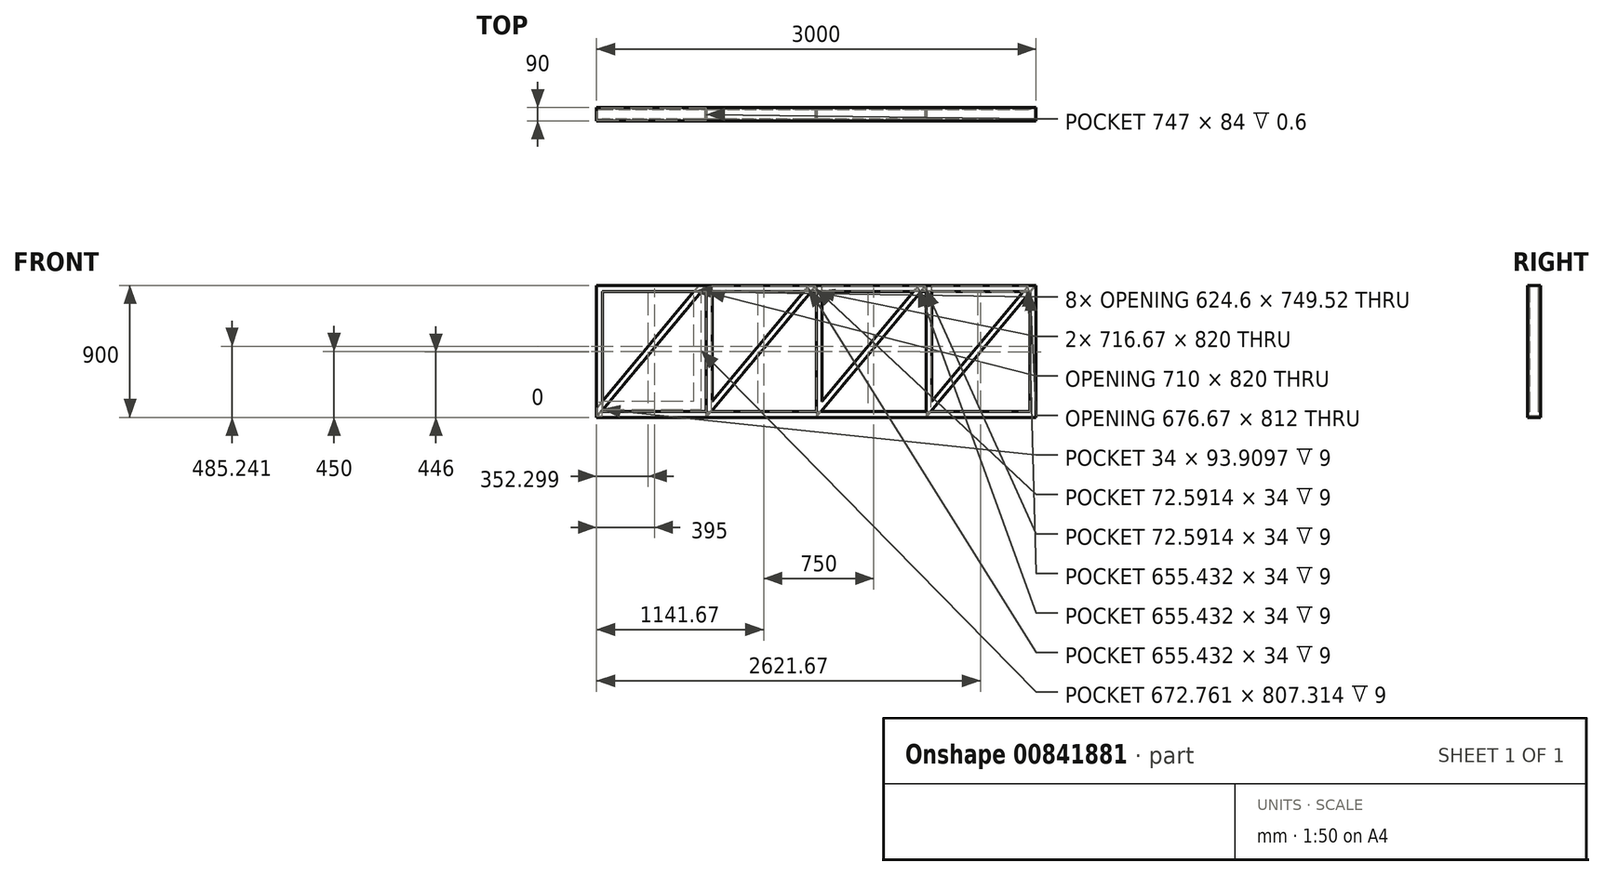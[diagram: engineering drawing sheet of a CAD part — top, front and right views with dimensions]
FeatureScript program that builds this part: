
annotation { "Feature Type Name" : "Feature", "Feature Type Description" : "" }
export const myFeature = defineFeature(function(context is Context, id is Id, definition is map)
    precondition{}
    {
        {
            var Q0;
            Q0=qCreatedBy(makeId("Front.planeOp"),FACE);
            var sketch = newSketch(context, id + "F0", { "sketchPlane" : qUnion([Q0])});
            skLineSegment(sketch, "E0.bottom", {"start": v(0, 0) * mm, "end": v(3000, 0) * mm});
            skLineSegment(sketch, "E0.top", {"start": v(0, 900) * mm, "end": v(3000, 900) * mm});
            skLineSegment(sketch, "E0.left", {"start": v(0, 0) * mm, "end": v(0, 900) * mm});
            skLineSegment(sketch, "E0.right", {"start": v(3000, 0) * mm, "end": v(3000, 900) * mm});
            skSolve(sketch);
        }
        {
            var Q0;
            Q0=qCreatedBy(makeId("Right.planeOp"),FACE);
            var sketch = newSketch(context, id + "F1", { "sketchPlane" : qUnion([Q0])});
            skLineSegment(sketch, "E1", {"start": v(0, 0) * mm, "end": v(-45, 0) * mm});
            skLineSegment(sketch, "E2", {"start": v(-45, 0) * mm, "end": v(-45, 40) * mm});
            skLineSegment(sketch, "E3", {"start": v(-45, 40) * mm, "end": v(-33, 40) * mm});
            skLineSegment(sketch, "E4.MirrorCS", {"start": v(45, 40) * mm, "end": v(33, 40) * mm});
            skLineSegment(sketch, "E5.MirrorCS", {"start": v(45, 0) * mm, "end": v(45, 40) * mm});
            skLineSegment(sketch, "E6.MirrorCS", {"start": v(0, 0) * mm, "end": v(45, 0) * mm});
            skLineSegment(sketch, "E7.0", {"start": v(42, 37) * mm, "end": v(33, 37) * mm});
            skLineSegment(sketch, "E7.1", {"start": v(42, 3) * mm, "end": v(42, 37) * mm});
            skLineSegment(sketch, "E7.2", {"start": v(-42, 37) * mm, "end": v(-33, 37) * mm});
            skLineSegment(sketch, "E7.3", {"start": v(-42, 3) * mm, "end": v(-42, 37) * mm});
            skLineSegment(sketch, "E7.4", {"start": v(0, 3) * mm, "end": v(-42, 3) * mm});
            skLineSegment(sketch, "E7.5", {"start": v(0, 3) * mm, "end": v(42, 3) * mm});
            skLineSegment(sketch, "E8", {"start": v(33, 40) * mm, "end": v(33, 37) * mm});
            skLineSegment(sketch, "E9", {"start": v(-33, 40) * mm, "end": v(-33, 37) * mm});
            skSolve(sketch);
        }
        {
            var Q0;
            Q0 = qSketchRegion(id + "F1", true);
            var Q1;
            Q1 = qConstructionFilter(qBodyType(qCreatedBy(id + "F0" ,EDGE), BodyType.WIRE), ConstructionObject.NO);
            sweep(context, id + "F2", {"profiles" : qUnion([Q0]), "path" : qUnion([Q1])});
        }
        {
            var Q0;
            Q0=qCreatedBy(makeId("Front.planeOp"),FACE);
            var sketch = newSketch(context, id + "F3", { "sketchPlane" : qUnion([Q0])});
            skLineSegment(sketch, "E10", {"start": v(0, 0) * mm, "end": v(750, 900) * mm});
            skLineSegment(sketch, "E11", {"start": v(750, 900) * mm, "end": v(750, 0) * mm});
            skLineSegment(sketch, "E12", {"start": v(750, 0) * mm, "end": v(1500, 900) * mm});
            skLineSegment(sketch, "E13", {"start": v(1500, 900) * mm, "end": v(1500, 0) * mm});
            skLineSegment(sketch, "E14", {"start": v(1500, 0) * mm, "end": v(2250, 900) * mm});
            skLineSegment(sketch, "E15", {"start": v(2250, 900) * mm, "end": v(2250, 0) * mm});
            skLineSegment(sketch, "E16", {"start": v(2250, 0) * mm, "end": v(3000, 900) * mm});
            skSolve(sketch);
        }
        {
            var Q0;
            Q0=makeQuery(id+"F2.opSweep","CAP_EDGE",EDGE,{"disambiguationData":[OSD([sQuery(id+"F0.wireOp",VERTEX,"E0.left.start"),sQuery(id+"F1.wireOp",EDGE,"E1"),sQuery(id+"F1.wireOp",EDGE,"E6.MirrorCS")])],"isStart":true});
            cPoint(context, id + "F4", {"entities" : qUnion([Q0]), "parameter" : 0.5});
        }
        {
            var Q0;
            Q0=sQuery(id+"F3.wireOp",EDGE,"E10");
            var Q1;
            Q1 = qCreatedBy(id + "F4" ,VERTEX);
            cPlane(context, id + "F5", {"entities" : qUnion([Q0, Q1]), "cplaneType" : CPlaneType.LINE_POINT, "offset" : 95 * mm, "width" : 150 * mm, "height" : 150 * mm});
        }
        {
            var Q0;
            Q0=qCreatedBy(id+"F5.planeOp",FACE);
            cPlane(context, id + "F6", {"entities" : qUnion([Q0]), "cplaneType" : CPlaneType.OFFSET, "offset" : 76.1 * mm, "width" : 150 * mm, "height" : 150 * mm});
        }
        {
            var Q0;
            Q0=qCreatedBy(id+"F6.planeOp",FACE);
            var sketch = newSketch(context, id + "F7", { "sketchPlane" : qUnion([Q0])});
            skLineSegment(sketch, "E17", {"start": v(0, 0) * mm, "end": v(0, -45) * mm});
            skLineSegment(sketch, "E18", {"start": v(0, -45) * mm, "end": v(-40, -45) * mm});
            skLineSegment(sketch, "E19", {"start": v(-40, -45) * mm, "end": v(-40, -33) * mm});
            skLineSegment(sketch, "E20", {"start": v(0, 0) * mm, "end": v(-36.54, 0) * mm, "construction": true});
            skLineSegment(sketch, "E21.MirrorCS", {"start": v(-40, 45) * mm, "end": v(-40, 33) * mm});
            skLineSegment(sketch, "E22.MirrorCS", {"start": v(0, 45) * mm, "end": v(-40, 45) * mm});
            skLineSegment(sketch, "E23.MirrorCS", {"start": v(0, 0) * mm, "end": v(0, 45) * mm});
            skLineSegment(sketch, "E24.0", {"start": v(-37, -42) * mm, "end": v(-37, -33) * mm});
            skLineSegment(sketch, "E24.1", {"start": v(-3, -42) * mm, "end": v(-37, -42) * mm});
            skLineSegment(sketch, "E24.2", {"start": v(-37, 42) * mm, "end": v(-37, 33) * mm});
            skLineSegment(sketch, "E24.3", {"start": v(-3, 42) * mm, "end": v(-37, 42) * mm});
            skLineSegment(sketch, "E24.4", {"start": v(-3, 0) * mm, "end": v(-3, 42) * mm});
            skLineSegment(sketch, "E24.5", {"start": v(-3, 0) * mm, "end": v(-3, -42) * mm});
            skLineSegment(sketch, "E25", {"start": v(-40, 33) * mm, "end": v(-37, 33) * mm});
            skLineSegment(sketch, "E26", {"start": v(-40, -33) * mm, "end": v(-37, -33) * mm});
            skSolve(sketch);
        }
        {
            var Q0;
            Q0 = qSketchRegion(id + "F7", true);
            var Q1;
            Q1 = qConstructionFilter(qBodyType(qCreatedBy(id + "F3" ,EDGE), BodyType.WIRE), ConstructionObject.NO);
            sweep(context, id + "F8", {"operationType" : NewBodyOperationType.ADD, "profiles" : qUnion([Q0]), "path" : qUnion([Q1])});
        }
        {
            var Q0;
            Q0=makeQuery(id+"F2.opSweep","SWEPT_FACE",FACE,{"disambiguationData":[OSD([sQuery(id+"F0.wireOp",EDGE,"E0.right"),sQuery(id+"F1.wireOp",EDGE,"E1"),sQuery(id+"F1.wireOp",EDGE,"E6.MirrorCS")])]});
            var sketch = newSketch(context, id + "F9", { "sketchPlane" : qUnion([Q0])});
            skLineSegment(sketch, "E27.bottom", {"start": v(-45, 900) * mm, "end": v(52.15, 900) * mm});
            skLineSegment(sketch, "E27.top", {"start": v(-45, 1018.86) * mm, "end": v(52.15, 1018.86) * mm});
            skLineSegment(sketch, "E27.left", {"start": v(-45, 900) * mm, "end": v(-45, 1018.86) * mm});
            skLineSegment(sketch, "E27.right", {"start": v(52.15, 900) * mm, "end": v(52.15, 1018.86) * mm});
            skSolve(sketch);
        }
        {
            var Q0;
            Q0 = qSketchRegion(id + "F9", true);
            extrude(context, id + "F10", {"entities" : qUnion([Q0]), "operationType" : NewBodyOperationType.REMOVE, "endBound" : BoundingType.THROUGH_ALL, "oppositeDirection" : true, "depth" : 25 * mm, "offsetDistance" : 25 * mm, "hasSecondDirection" : true, "secondDirectionOppositeDirection" : false, "secondDirectionDepth" : 25 * mm});
        }
        {
            var Q0;
            Q0=makeQuery(id+"F2.opSweep","SWEPT_FACE",FACE,{"disambiguationData":[OSD([sQuery(id+"F0.wireOp",EDGE,"E0.bottom"),sQuery(id+"F1.wireOp",EDGE,"E1"),sQuery(id+"F1.wireOp",EDGE,"E6.MirrorCS")])]});
            var sketch = newSketch(context, id + "F11", { "sketchPlane" : qUnion([Q0])});
            skLineSegment(sketch, "E28.bottom", {"start": v(0, 45) * mm, "end": v(-40.33, 45) * mm});
            skLineSegment(sketch, "E28.top", {"start": v(0, -45.94) * mm, "end": v(-40.33, -45.94) * mm});
            skLineSegment(sketch, "E28.left", {"start": v(0, 45) * mm, "end": v(0, -45.94) * mm});
            skLineSegment(sketch, "E28.right", {"start": v(-40.33, 45) * mm, "end": v(-40.33, -45.94) * mm});
            skSolve(sketch);
        }
        {
            var Q0;
            Q0 = qSketchRegion(id + "F11", true);
            extrude(context, id + "F12", {"entities" : qUnion([Q0]), "operationType" : NewBodyOperationType.REMOVE, "endBound" : BoundingType.THROUGH_ALL, "oppositeDirection" : true, "depth" : 25 * mm, "offsetDistance" : 25 * mm});
        }
    });
